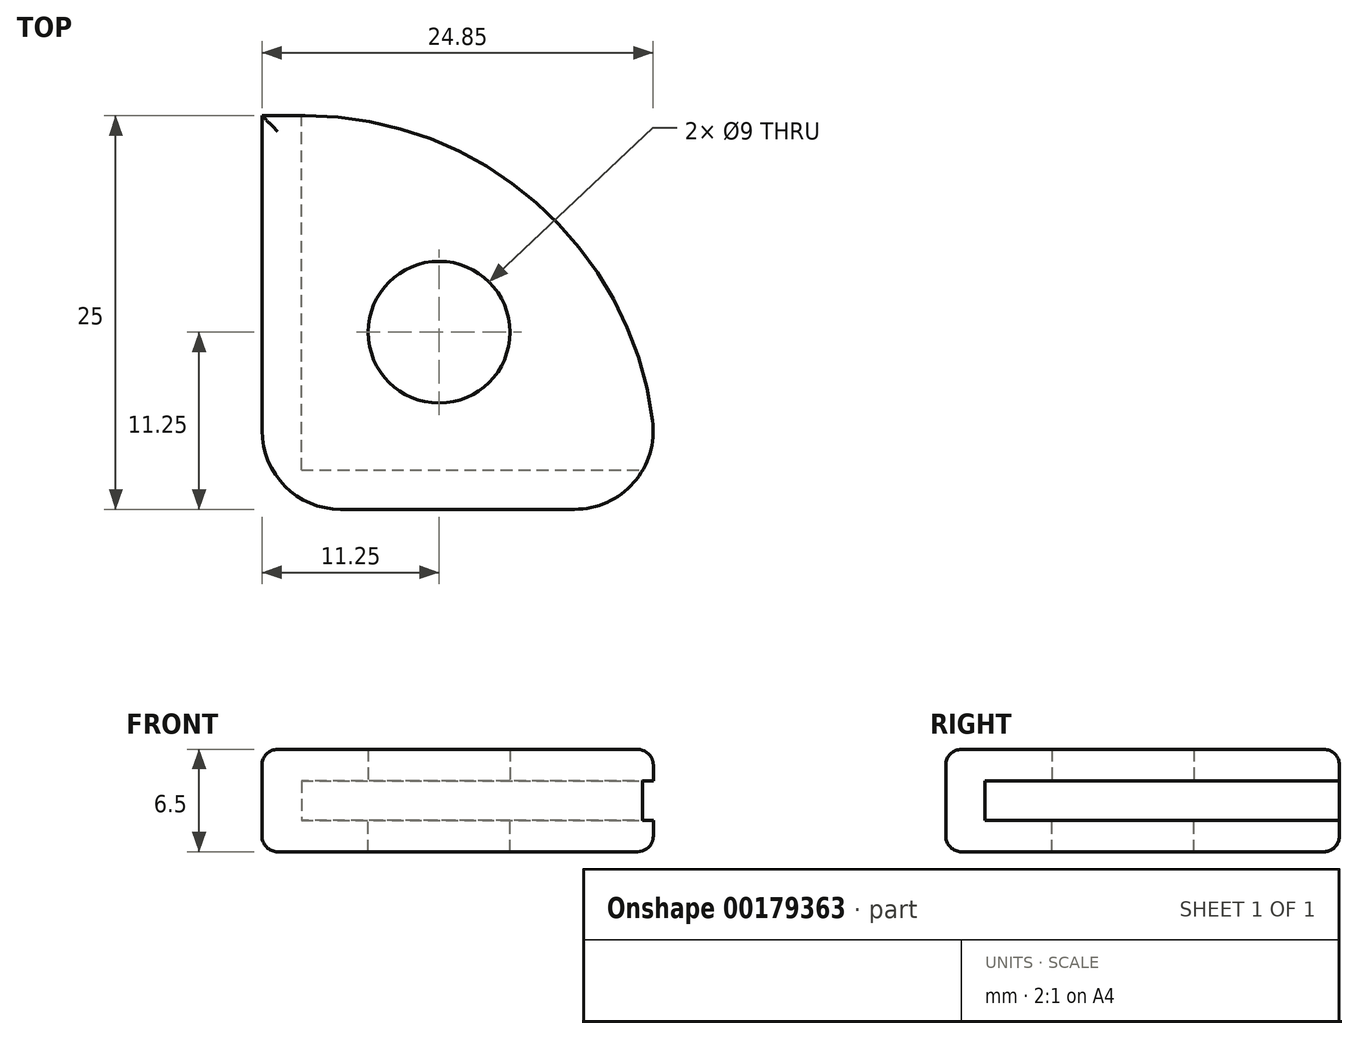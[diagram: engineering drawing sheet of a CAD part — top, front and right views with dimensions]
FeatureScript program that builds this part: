
annotation { "Feature Type Name" : "Feature", "Feature Type Description" : "" }
export const myFeature = defineFeature(function(context is Context, id is Id, definition is map)
    precondition{}
    {
        {
            var Q0;
            Q0=qCreatedBy(makeId("Top.planeOp"),FACE);
            var sketch = newSketch(context, id + "F0", { "sketchPlane" : qUnion([Q0])});
            skLineSegment(sketch, "E0.bottom", {"start": v(0, 0) * mm, "end": v(50, 0) * mm, "construction": true});
            skLineSegment(sketch, "E0.top", {"start": v(0, 50) * mm, "end": v(50, 50) * mm, "construction": true});
            skLineSegment(sketch, "E0.left", {"start": v(0, 0) * mm, "end": v(0, 50) * mm, "construction": true});
            skLineSegment(sketch, "E0.right", {"start": v(50, 0) * mm, "end": v(50, 50) * mm, "construction": true});
            skLineSegment(sketch, "E1.bottom", {"start": v(0, 0) * mm, "end": v(7.5, 0) * mm, "construction": true});
            skLineSegment(sketch, "E1.top", {"start": v(0, 9) * mm, "end": v(7.5, 9) * mm, "construction": true});
            skLineSegment(sketch, "E1.left", {"start": v(0, 0) * mm, "end": v(0, 9) * mm, "construction": true});
            skLineSegment(sketch, "E1.right", {"start": v(7.5, 0) * mm, "end": v(7.5, 9) * mm, "construction": true});
            skCircle(sketch, "E2", {"center": v(7.5, 9) * mm, "radius": 3 * mm, "construction": true});
            skLineSegment(sketch, "E3.bottom", {"start": v(0, 0) * mm, "end": v(9.5, 0) * mm, "construction": true});
            skLineSegment(sketch, "E3.top", {"start": v(0, 8) * mm, "end": v(9.5, 8) * mm, "construction": true});
            skLineSegment(sketch, "E3.left", {"start": v(0, 0) * mm, "end": v(0, 8) * mm, "construction": true});
            skLineSegment(sketch, "E3.right", {"start": v(9.5, 0) * mm, "end": v(9.5, 8) * mm, "construction": true});
            skCircle(sketch, "E4", {"center": v(9.5, 8) * mm, "radius": 3 * mm, "construction": true});
            skLineSegment(sketch, "E5.bottom", {"start": v(0, 0) * mm, "end": v(8.5, 0) * mm, "construction": true});
            skLineSegment(sketch, "E5.top", {"start": v(0, 8.5) * mm, "end": v(8.5, 8.5) * mm, "construction": true});
            skLineSegment(sketch, "E5.left", {"start": v(0, 0) * mm, "end": v(0, 8.5) * mm, "construction": true});
            skLineSegment(sketch, "E5.right", {"start": v(8.5, 0) * mm, "end": v(8.5, 8.5) * mm, "construction": true});
            skCircle(sketch, "E6", {"center": v(8.5, 8.5) * mm, "radius": 4.5 * mm});
            skLineSegment(sketch, "E7.bottom", {"start": v(-0.25, 0) * mm, "end": v(-2.75, 0) * mm});
            skLineSegment(sketch, "E7.top", {"start": v(-0.25, 22.25) * mm, "end": v(-2.75, 22.25) * mm});
            skLineSegment(sketch, "E7.left", {"start": v(-0.25, 0) * mm, "end": v(-0.25, 22.25) * mm});
            skLineSegment(sketch, "E7.right", {"start": v(-2.75, 0) * mm, "end": v(-2.75, 22.25) * mm});
            skLineSegment(sketch, "E8.bottom", {"start": v(-2.75, 0) * mm, "end": v(-0.25, 0) * mm});
            skLineSegment(sketch, "E8.top", {"start": v(-2.75, -2.75) * mm, "end": v(-0.25, -2.75) * mm});
            skLineSegment(sketch, "E8.left", {"start": v(-2.75, 0) * mm, "end": v(-2.75, -2.75) * mm});
            skLineSegment(sketch, "E8.right", {"start": v(-0.25, 0) * mm, "end": v(-0.25, -2.75) * mm});
            skLineSegment(sketch, "E9.bottom", {"start": v(-0.25, -2.75) * mm, "end": v(22.25, -2.75) * mm});
            skLineSegment(sketch, "E9.top", {"start": v(-0.25, -0.25) * mm, "end": v(22.25, -0.25) * mm});
            skLineSegment(sketch, "E9.left", {"start": v(-0.25, -2.75) * mm, "end": v(-0.25, -0.25) * mm});
            skLineSegment(sketch, "E9.right", {"start": v(22.25, -2.75) * mm, "end": v(22.25, -0.25) * mm});
            skArc(sketch, "E10", {"start": v(0, 22.25) * mm, "mid": v(15.73, 15.73) * mm, "end": v(22.25, 0) * mm});
            skLineSegment(sketch, "E11", {"start": v(22.25, -0.25) * mm, "end": v(22.25, 0) * mm});
            skLineSegment(sketch, "E12", {"start": v(-0.25, 22.25) * mm, "end": v(0, 22.25) * mm});
            skSolve(sketch);
        }
        {
            var Q0;
            Q0 = qSketchRegion(id + "F0", true);
            extrude(context, id + "F1", {"entities" : qUnion([Q0]), "oppositeDirection" : true, "depth" : 2 * mm, "offsetDistance" : 25 * mm});
        }
        {
            var Q0;
            Q0=makeQuery(id+"F0.imprint","IMPRINT",FACE,{"disambiguationData":[TD([[makeQuery(id+"F0.imprint","IMPRINT",EDGE,{"derivedFrom":sQuery(id+"F0.wireOp",EDGE,"E7.bottom")}),-1.0]])]});
            var Q1;
            {var subQ3=sQuery(id+"F0.wireOp",EDGE,"E7.bottom");Q1=makeQuery(id+"F0.imprint","IMPRINT",FACE,{"disambiguationData":[TD([[makeQuery(id+"F0.imprint","IMPRINT",EDGE,{"derivedFrom":subQ3}),1.0]])]});}
            var Q2;
            {var subQ0=sQuery(id+"F0.wireOp",EDGE,"E9.bottom");Q2=makeQuery(id+"F0.imprint","IMPRINT",FACE,{"disambiguationData":[TD([[makeQuery(id+"F0.imprint","IMPRINT",EDGE,{"derivedFrom":subQ0}),1.0]])]});}
            extrude(context, id + "F2", {"entities" : qUnion([Q0, Q1, Q2]), "operationType" : NewBodyOperationType.ADD, "depth" : 2.5 * mm, "offsetDistance" : 25 * mm});
        }
        {
            var Q0;
            Q0=makeQuery(id+"F2.opExtrude","CAP_FACE",FACE,{"disambiguationData":[OSD([sQuery(id+"F0.wireOp",EDGE,"E7.top"),sQuery(id+"F0.wireOp",EDGE,"E7.left"),sQuery(id+"F0.wireOp",EDGE,"E7.right"),sQuery(id+"F0.wireOp",EDGE,"E8.top"),sQuery(id+"F0.wireOp",EDGE,"E8.left"),sQuery(id+"F0.wireOp",EDGE,"E8.right"),sQuery(id+"F0.wireOp",EDGE,"E9.bottom"),sQuery(id+"F0.wireOp",EDGE,"E9.top"),sQuery(id+"F0.wireOp",EDGE,"E9.right")])],"isStart":false});
            var sketch = newSketch(context, id + "F3", { "sketchPlane" : qUnion([Q0])});
            skLineSegment(sketch, "E13.bottom", {"start": v(-2.75, 22.25) * mm, "end": v(-0.25, 22.25) * mm});
            skLineSegment(sketch, "E13.top", {"start": v(-2.75, -2.75) * mm, "end": v(-0.25, -2.75) * mm});
            skLineSegment(sketch, "E13.left", {"start": v(-2.75, 22.25) * mm, "end": v(-2.75, -2.75) * mm});
            skLineSegment(sketch, "E13.right", {"start": v(-0.25, 22.25) * mm, "end": v(-0.25, -2.75) * mm});
            skLineSegment(sketch, "E14.bottom", {"start": v(-2.75, -2.75) * mm, "end": v(22.25, -2.75) * mm});
            skLineSegment(sketch, "E14.top", {"start": v(-2.75, -0.25) * mm, "end": v(22.25, -0.25) * mm});
            skLineSegment(sketch, "E14.left", {"start": v(-2.75, -2.75) * mm, "end": v(-2.75, -0.25) * mm});
            skLineSegment(sketch, "E14.right", {"start": v(22.25, -2.75) * mm, "end": v(22.25, -0.25) * mm});
            skArc(sketch, "E15", {"start": v(0, 22.25) * mm, "mid": v(15.73, 15.73) * mm, "end": v(22.25, 0) * mm});
            skLineSegment(sketch, "E16", {"start": v(-0.25, 22.25) * mm, "end": v(0, 22.25) * mm});
            skLineSegment(sketch, "E17", {"start": v(22.25, -0.25) * mm, "end": v(22.25, 0) * mm});
            skCircle(sketch, "E18", {"center": v(8.5, 8.5) * mm, "radius": 4.5 * mm});
            skSolve(sketch);
        }
        {
            var Q0;
            Q0 = qSketchRegion(id + "F3", true);
            extrude(context, id + "F4", {"entities" : qUnion([Q0]), "operationType" : NewBodyOperationType.ADD, "depth" : 2 * mm, "offsetDistance" : 25 * mm});
        }
        {
            var Q0;
            {var subQ0=sQuery(id+"F0.wireOp",EDGE,"E8.left");var subQ1=sQuery(id+"F0.wireOp",EDGE,"E8.top");Q0=makeQuery(id+"F4.boolean.opBoolean","MERGE",EDGE,{"derivedFrom":[makeQuery(id+"F2.boolean.opBoolean","MERGE",EDGE,{"derivedFrom":[makeQuery(id+"F1.opExtrude","SWEPT_EDGE",EDGE,{"disambiguationData":[OSD([subQ1,subQ0])]}),makeQuery(id+"F2.opExtrude","SWEPT_EDGE",EDGE,{"disambiguationData":[OSD([subQ1,subQ0])]})]}),makeQuery(id+"F4.opExtrude","SWEPT_EDGE",EDGE,{"disambiguationData":[OSD([sQuery(id+"F3.wireOp",EDGE,"E14.bottom"),sQuery(id+"F3.wireOp",EDGE,"E14.left")])]})]});}
            fillet(context, id + "F5", {"entities" : qUnion([Q0]), "tangentPropagation" : true, "radius" : 5 * mm, "defaultsChanged" : false, "vertexSettings" : [], "allowEdgeOverflow" : false});
        }
        {
            var Q0;
            Q0=makeQuery(id+"F4.opExtrude","CAP_EDGE",EDGE,{"disambiguationData":[OSD([sQuery(id+"F3.wireOp",EDGE,"E14.bottom")])],"isStart":false});
            var Q1;
            Q1=makeQuery(id+"F1.opExtrude","CAP_EDGE",EDGE,{"disambiguationData":[OSD([sQuery(id+"F0.wireOp",EDGE,"E8.top"),sQuery(id+"F0.wireOp",EDGE,"E9.bottom")])],"isStart":false});
            var Q2;
            {var subQ0=sQuery(id+"F0.wireOp",EDGE,"E8.left");var subQ1=sQuery(id+"F0.wireOp",EDGE,"E8.top");Q2=makeQuery(id+"F5.opFillet","BLEND_EDGE",EDGE,{"blendedFrom":[makeQuery(id+"F4.boolean.opBoolean","MERGE",EDGE,{"derivedFrom":[makeQuery(id+"F2.boolean.opBoolean","MERGE",EDGE,{"derivedFrom":[makeQuery(id+"F1.opExtrude","SWEPT_EDGE",EDGE,{"disambiguationData":[OSD([subQ1,subQ0])]}),makeQuery(id+"F2.opExtrude","SWEPT_EDGE",EDGE,{"disambiguationData":[OSD([subQ1,subQ0])]})]}),makeQuery(id+"F4.opExtrude","SWEPT_EDGE",EDGE,{"disambiguationData":[OSD([sQuery(id+"F3.wireOp",EDGE,"E14.bottom"),sQuery(id+"F3.wireOp",EDGE,"E14.left")])]})]}),makeQuery(id+"F1.opExtrude","CAP_FACE",FACE,{"disambiguationData":[OSD([sQuery(id+"F0.wireOp",EDGE,"E6"),sQuery(id+"F0.wireOp",EDGE,"E7.top"),sQuery(id+"F0.wireOp",EDGE,"E7.right"),subQ1,subQ0,sQuery(id+"F0.wireOp",EDGE,"E9.bottom"),sQuery(id+"F0.wireOp",EDGE,"E9.right"),sQuery(id+"F0.wireOp",EDGE,"E10"),sQuery(id+"F0.wireOp",EDGE,"E11"),sQuery(id+"F0.wireOp",EDGE,"E12")])],"isStart":false})],"blendedInto":[makeQuery(id+"F1.opExtrude","CAP_FACE",FACE,{"disambiguationData":[OSD([sQuery(id+"F0.wireOp",EDGE,"E6"),sQuery(id+"F0.wireOp",EDGE,"E7.top"),sQuery(id+"F0.wireOp",EDGE,"E7.right"),subQ1,subQ0,sQuery(id+"F0.wireOp",EDGE,"E9.bottom"),sQuery(id+"F0.wireOp",EDGE,"E9.right"),sQuery(id+"F0.wireOp",EDGE,"E10"),sQuery(id+"F0.wireOp",EDGE,"E11"),sQuery(id+"F0.wireOp",EDGE,"E12")])],"isStart":false})]});}
            fillet(context, id + "F6", {"entities" : qUnion([Q0, Q1, Q2]), "tangentPropagation" : true, "radius" : 1 * mm, "defaultsChanged" : true, "vertexSettings" : [], "allowEdgeOverflow" : false});
        }
    });
